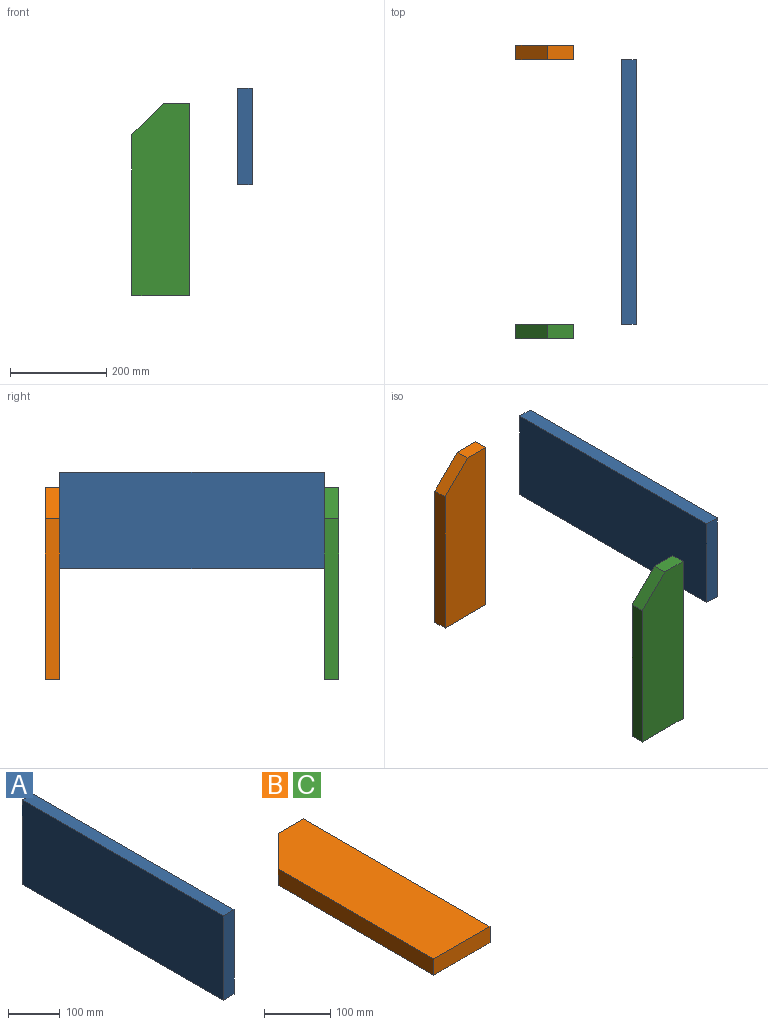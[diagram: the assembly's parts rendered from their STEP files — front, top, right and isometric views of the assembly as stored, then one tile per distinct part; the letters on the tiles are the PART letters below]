
ASSEMBLY  parts=3 mates=3
PART A: 6 faces, bbox 30x550x200 mm
  f0: plane 550x200mm, normal (1,0,0), area 110000mm2, adj f1,f3,f4,f5
  f1: plane 550x30mm, normal (0,0,-1), area 16500mm2, adj f0,f2,f4,f5
  f2: plane 550x200mm, normal (-1,0,0), area 110000mm2, adj f1,f3,f4,f5
  f3: plane 550x30mm, normal (0,0,1), area 16500mm2, adj f0,f2,f4,f5
  f4: plane 200x30mm, normal (0,1,0), area 6000mm2, adj f0,f1,f2,f3
  f5: plane 200x30mm, normal (0,-1,0), area 6000mm2, adj f0,f1,f2,f3
PART B: 7 faces, bbox 120x400x30 mm
  f0: plane 334.09x30mm, normal (-1,0,0), area 10022.8mm2, adj f1,f4,f5,f6
  f1: plane 120x30mm, normal (0,-1,0), area 3600mm2, adj f0,f2,f5,f6
  f2: plane 400x30mm, normal (1,0,0), area 12000mm2, adj f1,f3,f5,f6
  f3: plane 54.09x30mm, normal (0,1,0), area 1622.8mm2, adj f2,f4,f5,f6
  f4: plane 65.91x65.91mm, normal (-0.71,0.71,0), area 2796.2mm2, adj f0,f3,f5,f6
  f5: plane 400x120mm, normal (0,0,1), area 45828.2mm2, adj f0,f1,f2,f3,f4
  f6: plane 400x120mm, normal (0,0,-1), area 45828.2mm2, adj f0,f1,f2,f3,f4
PART C: same geometry as B
PLACE A t=(101.75,0,-107.5)mm
PLACE B rot(axis=(1,0,0),90deg) t=(382.68,671.18,-448.21)mm
PLACE C rot(axis=(1,0,0),90deg) t=(382.68,91.18,-448.21)mm
MATE planar B.f2 <-> C.f2  axis (1,0,0) through (385.9,656.18,-386.15)mm
MATE planar B.f5 <-> A.f4  axis (0,-1,0) through (327.71,641.18,-394.59)mm
MATE planar C.f1 <-> B.f1  axis (0,0,-1) through (325.9,76.18,-586.15)mm
